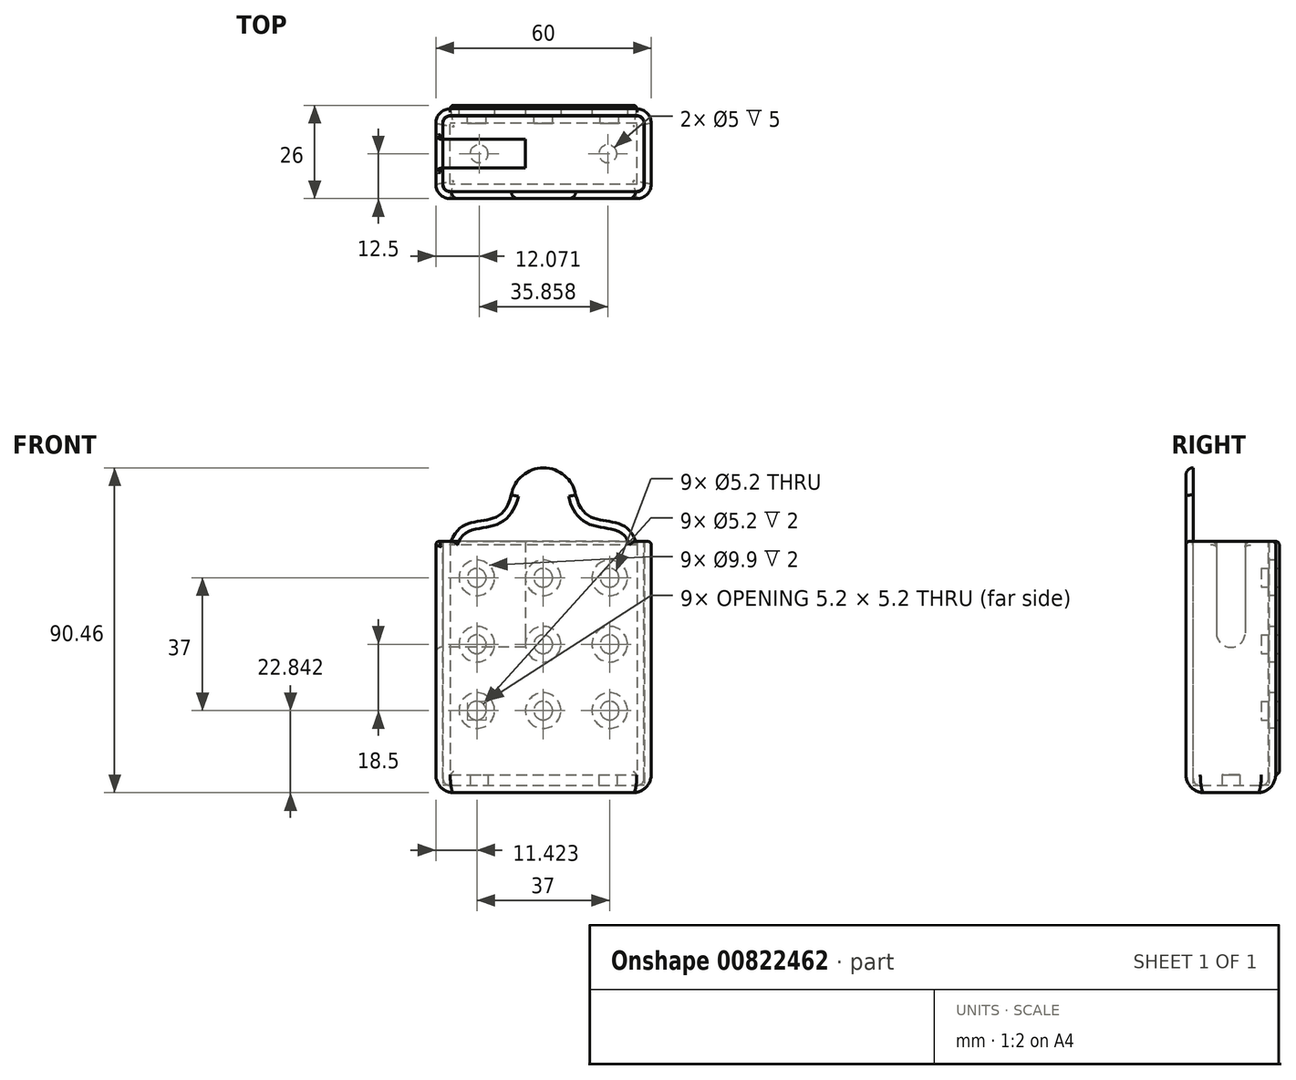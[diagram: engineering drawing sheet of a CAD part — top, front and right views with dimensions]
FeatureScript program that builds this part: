
annotation { "Feature Type Name" : "Feature", "Feature Type Description" : "" }
export const myFeature = defineFeature(function(context is Context, id is Id, definition is map)
    precondition{}
    {
        {
            var Q0;
            Q0=qCreatedBy(makeId("Front.planeOp"),FACE);
            var sketch = newSketch(context, id + "F0", { "sketchPlane" : qUnion([Q0])});
            skPoint(sketch, "E0.middle", {"position": v(0, 0) * mm});
            skLineSegment(sketch, "E1.bottom", {"start": v(28, -42.5) * mm, "end": v(-28, -42.5) * mm});
            skLineSegment(sketch, "E1.top", {"start": v(28, 42.5) * mm, "end": v(-28, 42.5) * mm});
            skLineSegment(sketch, "E1.left", {"start": v(28, -42.5) * mm, "end": v(28, 42.5) * mm});
            skLineSegment(sketch, "E1.right", {"start": v(-28, -42.5) * mm, "end": v(-28, 42.5) * mm});
            skSolve(sketch);
        }
        {
            var Q0;
            Q0=qSketchRegion(id+"F0",true);
            extrude(context, id + "F1", {"entities" : qUnion([Q0]), "endBound" : BoundingType.SYMMETRIC, "depth" : 21 * mm, "offsetDistance" : 25 * mm});
        }
        {
            var Q0;
            Q0=makeQuery(id+"F1.opExtrude","CAP_FACE",FACE,{"disambiguationData":[OSD([sQuery(id+"F0.wireOp",EDGE,"E1.bottom"),sQuery(id+"F0.wireOp",EDGE,"E1.top"),sQuery(id+"F0.wireOp",EDGE,"E1.left"),sQuery(id+"F0.wireOp",EDGE,"E1.right")])],"isStart":false});
            var Q1;
            Q1=makeQuery(id+"F1.opExtrude","CAP_FACE",FACE,{"disambiguationData":[OSD([sQuery(id+"F0.wireOp",EDGE,"E1.bottom"),sQuery(id+"F0.wireOp",EDGE,"E1.top"),sQuery(id+"F0.wireOp",EDGE,"E1.left"),sQuery(id+"F0.wireOp",EDGE,"E1.right")])],"isStart":true});
            var Q2;
            Q2=makeQuery(id+"F1.opExtrude","SWEPT_EDGE",EDGE,{"disambiguationData":[OSD([sQuery(id+"F0.wireOp",EDGE,"E1.bottom"),sQuery(id+"F0.wireOp",EDGE,"E1.left")])]});
            var Q3;
            Q3=makeQuery(id+"F1.opExtrude","SWEPT_EDGE",EDGE,{"disambiguationData":[OSD([sQuery(id+"F0.wireOp",EDGE,"E1.bottom"),sQuery(id+"F0.wireOp",EDGE,"E1.right")])]});
            var Q4;
            Q4=makeQuery(id+"F1.opExtrude","SWEPT_FACE",FACE,{"disambiguationData":[OSD([sQuery(id+"F0.wireOp",EDGE,"E1.top")])]});
            fillet(context, id + "F2", {"entities" : qUnion([Q0, Q1, Q2, Q3, Q4]), "radius" : 2 * mm, "tangentPropagation" : true, "allowEdgeOverflow" : false});
        }
        {
            var Q0;
            Q0=qCreatedBy(makeId("Top.planeOp"),FACE);
            var sketch = newSketch(context, id + "F3", { "sketchPlane" : qUnion([Q0])});
            skArc(sketch, "E2.0", {"start": v(-26, 12.5) * mm, "mid": v(-28.83, 11.33) * mm, "end": v(-30, 8.5) * mm});
            skLineSegment(sketch, "E2.1", {"start": v(-30, -8.5) * mm, "end": v(-30, 8.5) * mm});
            skLineSegment(sketch, "E2.2", {"start": v(-26, 12.5) * mm, "end": v(26, 12.5) * mm});
            skArc(sketch, "E2.3", {"start": v(-30, -8.5) * mm, "mid": v(-28.83, -11.33) * mm, "end": v(-26, -12.5) * mm});
            skArc(sketch, "E2.4", {"start": v(30, 8.5) * mm, "mid": v(28.83, 11.33) * mm, "end": v(26, 12.5) * mm});
            skLineSegment(sketch, "E2.5", {"start": v(30, 8.5) * mm, "end": v(30, -8.5) * mm});
            skArc(sketch, "E2.6", {"start": v(26, -12.5) * mm, "mid": v(28.83, -11.33) * mm, "end": v(30, -8.5) * mm});
            skLineSegment(sketch, "E2.7", {"start": v(26, -12.5) * mm, "end": v(-26, -12.5) * mm});
            skArc(sketch, "E3.0", {"start": v(-26, 10.6) * mm, "mid": v(-27.48, 9.98) * mm, "end": v(-28.1, 8.5) * mm});
            skLineSegment(sketch, "E3.1", {"start": v(-28.1, -8.5) * mm, "end": v(-28.1, 8.5) * mm});
            skLineSegment(sketch, "E3.2", {"start": v(-26, 10.6) * mm, "end": v(26, 10.6) * mm});
            skArc(sketch, "E3.3", {"start": v(-28.1, -8.5) * mm, "mid": v(-27.48, -9.98) * mm, "end": v(-26, -10.6) * mm});
            skArc(sketch, "E3.4", {"start": v(28.1, 8.5) * mm, "mid": v(27.48, 9.98) * mm, "end": v(26, 10.6) * mm});
            skLineSegment(sketch, "E3.5", {"start": v(28.1, 8.5) * mm, "end": v(28.1, -8.5) * mm});
            skArc(sketch, "E3.6", {"start": v(26, -10.6) * mm, "mid": v(27.48, -9.98) * mm, "end": v(28.1, -8.5) * mm});
            skLineSegment(sketch, "E3.7", {"start": v(26, -10.6) * mm, "end": v(-26, -10.6) * mm});
            skSolve(sketch);
        }
        {
            var Q0;
            Q0=makeQuery(id+"F3.imprint","IMPRINT",FACE,{"disambiguationData":[TD([[makeQuery(id+"F3.imprint","IMPRINT",EDGE,{"derivedFrom":sQuery(id+"F3.wireOp",EDGE,"E2.0")}),1.0]])]});
            extrude(context, id + "F4", {"entities" : qUnion([Q0]), "endBound" : BoundingType.SYMMETRIC, "depth" : 85 * mm, "offsetDistance" : 25 * mm});
        }
        {
            var Q0;
            Q0=makeQuery(id+"F4.opExtrude","CAP_FACE",FACE,{"disambiguationData":[OSD([sQuery(id+"F3.wireOp",EDGE,"E2.0"),sQuery(id+"F3.wireOp",EDGE,"E2.1"),sQuery(id+"F3.wireOp",EDGE,"E2.2"),sQuery(id+"F3.wireOp",EDGE,"E2.3"),sQuery(id+"F3.wireOp",EDGE,"E2.4"),sQuery(id+"F3.wireOp",EDGE,"E2.5"),sQuery(id+"F3.wireOp",EDGE,"E2.6"),sQuery(id+"F3.wireOp",EDGE,"E2.7"),sQuery(id+"F3.wireOp",EDGE,"E3.0"),sQuery(id+"F3.wireOp",EDGE,"E3.1"),sQuery(id+"F3.wireOp",EDGE,"E3.2"),sQuery(id+"F3.wireOp",EDGE,"E3.3"),sQuery(id+"F3.wireOp",EDGE,"E3.4"),sQuery(id+"F3.wireOp",EDGE,"E3.5"),sQuery(id+"F3.wireOp",EDGE,"E3.6"),sQuery(id+"F3.wireOp",EDGE,"E3.7")])],"isStart":true});
            var sketch = newSketch(context, id + "F5", { "sketchPlane" : qUnion([Q0])});
            skArc(sketch, "E4.0", {"start": v(30, 8.5) * mm, "mid": v(28.83, 11.33) * mm, "end": v(26, 12.5) * mm});
            skLineSegment(sketch, "E4.1", {"start": v(30, -8.5) * mm, "end": v(30, 8.5) * mm});
            skLineSegment(sketch, "E4.2", {"start": v(26, 12.5) * mm, "end": v(-26, 12.5) * mm});
            skArc(sketch, "E4.3", {"start": v(26, -12.5) * mm, "mid": v(28.83, -11.33) * mm, "end": v(30, -8.5) * mm});
            skArc(sketch, "E4.4", {"start": v(-26, 12.5) * mm, "mid": v(-28.83, 11.33) * mm, "end": v(-30, 8.5) * mm});
            skLineSegment(sketch, "E4.5", {"start": v(-30, 8.5) * mm, "end": v(-30, -8.5) * mm});
            skArc(sketch, "E4.6", {"start": v(-30, -8.5) * mm, "mid": v(-28.83, -11.33) * mm, "end": v(-26, -12.5) * mm});
            skLineSegment(sketch, "E4.7", {"start": v(-26, -12.5) * mm, "end": v(26, -12.5) * mm});
            skSolve(sketch);
        }
        {
            var Q0;
            Q0 = qSketchRegion(id + "F5", true);
            extrude(context, id + "F6", {"entities" : qUnion([Q0]), "operationType" : NewBodyOperationType.ADD, "depth" : 2 * mm, "offsetDistance" : 25 * mm});
        }
        {
            var Q0;
            Q0=makeQuery(id+"F6.opExtrude","CAP_FACE",FACE,{"disambiguationData":[OSD([sQuery(id+"F5.wireOp",EDGE,"E4.0"),sQuery(id+"F5.wireOp",EDGE,"E4.1"),sQuery(id+"F5.wireOp",EDGE,"E4.2"),sQuery(id+"F5.wireOp",EDGE,"E4.3"),sQuery(id+"F5.wireOp",EDGE,"E4.4"),sQuery(id+"F5.wireOp",EDGE,"E4.5"),sQuery(id+"F5.wireOp",EDGE,"E4.6"),sQuery(id+"F5.wireOp",EDGE,"E4.7")])],"isStart":false});
            fillet(context, id + "F7", {"entities" : qUnion([Q0]), "radius" : 5 * mm, "tangentPropagation" : true, "allowEdgeOverflow" : false});
        }
        {
            var Q0;
            Q0=qCreatedBy(makeId("Front.planeOp"),FACE);
            var sketch = newSketch(context, id + "F8", { "sketchPlane" : qUnion([Q0])});
            skLineSegment(sketch, "E5.bottom", {"start": v(-62.47, 73.93) * mm, "end": v(54.88, 73.93) * mm});
            skLineSegment(sketch, "E5.top", {"start": v(-62.47, 25.5) * mm, "end": v(54.88, 25.5) * mm});
            skLineSegment(sketch, "E5.left", {"start": v(-62.47, 73.93) * mm, "end": v(-62.47, 25.5) * mm});
            skLineSegment(sketch, "E5.right", {"start": v(54.88, 73.93) * mm, "end": v(54.88, 25.5) * mm});
            skSolve(sketch);
        }
        {
            var Q0;
            Q0 = qSketchRegion(id + "F8", true);
            extrude(context, id + "F9", {"entities" : qUnion([Q0]), "operationType" : NewBodyOperationType.REMOVE, "depth" : 25 * mm, "offsetDistance" : 25 * mm, "hasSecondDirection" : true, "secondDirectionOppositeDirection" : true, "secondDirectionDepth" : 25 * mm});
        }
        {
            var Q0;
            Q0=makeQuery(id+"F6.boolean.opBoolean","MERGE",FACE,{"derivedFrom":[makeQuery(id+"F4.opExtrude","SWEPT_FACE",FACE,{"disambiguationData":[OSD([sQuery(id+"F3.wireOp",EDGE,"E2.2")])]}),makeQuery(id+"F6.opExtrude","SWEPT_FACE",FACE,{"disambiguationData":[OSD([sQuery(id+"F5.wireOp",EDGE,"E4.7")])]})]});
            var sketch = newSketch(context, id + "F10", { "sketchPlane" : qUnion([Q0])});
            skLineSegment(sketch, "E6.bottom", {"start": v(-26, 25.52) * mm, "end": v(26, 25.52) * mm});
            skLineSegment(sketch, "E6.top", {"start": v(-26, -39.5) * mm, "end": v(26, -39.5) * mm});
            skLineSegment(sketch, "E6.left", {"start": v(-26, 25.52) * mm, "end": v(-26, -39.5) * mm});
            skLineSegment(sketch, "E6.right", {"start": v(26, 25.52) * mm, "end": v(26, -39.5) * mm});
            skSolve(sketch);
        }
        {
            var Q0;
            Q0 = qSketchRegion(id + "F10", true);
            extrude(context, id + "F11", {"entities" : qUnion([Q0]), "operationType" : NewBodyOperationType.ADD, "depth" : 1 * mm, "offsetDistance" : 25 * mm});
        }
        {
            var Q0;
            Q0=makeQuery(id+"F11.opExtrude","CAP_FACE",FACE,{"disambiguationData":[OSD([sQuery(id+"F10.wireOp",EDGE,"E6.bottom"),sQuery(id+"F10.wireOp",EDGE,"E6.top"),sQuery(id+"F10.wireOp",EDGE,"E6.left"),sQuery(id+"F10.wireOp",EDGE,"E6.right")])],"isStart":false});
            var sketch = newSketch(context, id + "F12", { "sketchPlane" : qUnion([Q0])});
            skCircle(sketch, "E7", {"center": v(-18.42, 15.34) * mm, "radius": 2.6 * mm});
            skCircle(sketch, "E8.0.1.0", {"center": v(-18.42, -3.16) * mm, "radius": 2.6 * mm});
            skCircle(sketch, "E8.0.2.0", {"center": v(-18.42, -21.66) * mm, "radius": 2.6 * mm});
            skCircle(sketch, "E8.1.0.0", {"center": v(0.08, 15.34) * mm, "radius": 2.6 * mm});
            skCircle(sketch, "E8.1.1.0", {"center": v(0.08, -3.16) * mm, "radius": 2.6 * mm});
            skCircle(sketch, "E8.1.2.0", {"center": v(0.08, -21.66) * mm, "radius": 2.6 * mm});
            skCircle(sketch, "E8.2.0.0", {"center": v(18.58, 15.34) * mm, "radius": 2.6 * mm});
            skCircle(sketch, "E8.2.1.0", {"center": v(18.58, -3.16) * mm, "radius": 2.6 * mm});
            skCircle(sketch, "E8.2.2.0", {"center": v(18.58, -21.66) * mm, "radius": 2.6 * mm});
            skLineSegment(sketch, "E8.direction1", {"start": v(-18.42, 15.34) * mm, "end": v(0.08, 15.34) * mm, "construction": true});
            skLineSegment(sketch, "E8.direction2", {"start": v(-18.42, 15.34) * mm, "end": v(-18.42, -3.16) * mm, "construction": true});
            skSolve(sketch);
        }
        {
            var Q0;
            Q0 = qSketchRegion(id + "F12", true);
            extrude(context, id + "F13", {"entities" : qUnion([Q0]), "operationType" : NewBodyOperationType.REMOVE, "oppositeDirection" : true, "depth" : 5 * mm, "offsetDistance" : 25 * mm});
        }
        {
            var Q0;
            Q0=makeQuery(id+"F6.opExtrude","CAP_FACE",FACE,{"disambiguationData":[OSD([sQuery(id+"F5.wireOp",EDGE,"E4.0"),sQuery(id+"F5.wireOp",EDGE,"E4.1"),sQuery(id+"F5.wireOp",EDGE,"E4.2"),sQuery(id+"F5.wireOp",EDGE,"E4.3"),sQuery(id+"F5.wireOp",EDGE,"E4.4"),sQuery(id+"F5.wireOp",EDGE,"E4.5"),sQuery(id+"F5.wireOp",EDGE,"E4.6"),sQuery(id+"F5.wireOp",EDGE,"E4.7")])],"isStart":false});
            var sketch = newSketch(context, id + "F14", { "sketchPlane" : qUnion([Q0])});
            skCircle(sketch, "E9", {"center": v(-17.93, 0) * mm, "radius": 2.5 * mm});
            skCircle(sketch, "E10.MirrorC", {"center": v(17.93, 0) * mm, "radius": 2.5 * mm});
            skSolve(sketch);
        }
        {
            var Q0;
            Q0 = qSketchRegion(id + "F14", true);
            extrude(context, id + "F15", {"entities" : qUnion([Q0]), "operationType" : NewBodyOperationType.REMOVE, "oppositeDirection" : true, "depth" : 5 * mm, "offsetDistance" : 25 * mm});
        }
        {
            var Q0;
            Q0=makeQuery(id+"F9.boolean.opBoolean","INTERSECT",EDGE,{"derivedFrom":[makeQuery(id+"F6.boolean.opBoolean","MERGE",FACE,{"derivedFrom":[makeQuery(id+"F4.opExtrude","SWEPT_FACE",FACE,{"disambiguationData":[OSD([sQuery(id+"F3.wireOp",EDGE,"E2.7")])]}),makeQuery(id+"F6.opExtrude","SWEPT_FACE",FACE,{"disambiguationData":[OSD([sQuery(id+"F5.wireOp",EDGE,"E4.2")])]})]}),makeQuery(id+"F9.opExtrude","SWEPT_FACE",FACE,{"disambiguationData":[OSD([sQuery(id+"F8.wireOp",EDGE,"E5.top")])]})]});
            fillet(context, id + "F16", {"entities" : qUnion([Q0]), "radius" : 1 * mm, "tangentPropagation" : true, "allowEdgeOverflow" : false});
        }
        {
            var Q0;
            Q0=makeQuery(id+"F6.boolean.opBoolean","MERGE",FACE,{"derivedFrom":[makeQuery(id+"F4.opExtrude","SWEPT_FACE",FACE,{"disambiguationData":[OSD([sQuery(id+"F3.wireOp",EDGE,"E2.1")])]}),makeQuery(id+"F6.opExtrude","SWEPT_FACE",FACE,{"disambiguationData":[OSD([sQuery(id+"F5.wireOp",EDGE,"E4.5")])]})]});
            var sketch = newSketch(context, id + "F17", { "sketchPlane" : qUnion([Q0])});
            skLineSegment(sketch, "E11", {"start": v(0, 31.44) * mm, "end": v(0, 0) * mm, "construction": true});
            skArc(sketch, "E12.0.startCap", {"start": v(-4, 31.44) * mm, "mid": v(0, 35.44) * mm, "end": v(4, 31.44) * mm});
            skArc(sketch, "E12.0.endCap", {"start": v(4, 0) * mm, "mid": v(0, -4) * mm, "end": v(-4, 0) * mm});
            skLineSegment(sketch, "E12.0.left", {"start": v(4, 31.44) * mm, "end": v(4, 0) * mm});
            skLineSegment(sketch, "E12.0.right", {"start": v(-4, 31.44) * mm, "end": v(-4, 0) * mm});
            skSolve(sketch);
        }
        {
            var Q0;
            Q0 = qSketchRegion(id + "F17", true);
            extrude(context, id + "F18", {"entities" : qUnion([Q0]), "operationType" : NewBodyOperationType.REMOVE, "oppositeDirection" : true, "depth" : 25 * mm, "offsetDistance" : 25 * mm});
        }
        {
            var Q0;
            Q0=makeQuery(id+"F18.boolean.opBoolean","INTERSECT",EDGE,{"derivedFrom":[makeQuery(id+"F9.boolean.opBoolean","COPY",FACE,{"disambiguationData":[TD([makeQuery(id+"F4.opExtrude","SWEPT_FACE",FACE,{"disambiguationData":[OSD([sQuery(id+"F3.wireOp",EDGE,"E2.0")])]})])],"derivedFrom":makeQuery(id+"F9.opExtrude","SWEPT_FACE",FACE,{"disambiguationData":[OSD([sQuery(id+"F8.wireOp",EDGE,"E5.top")])]})}),makeQuery(id+"F18.opExtrude","SWEPT_FACE",FACE,{"disambiguationData":[OSD([sQuery(id+"F17.wireOp",EDGE,"E12.0.right")])]})]});
            fillet(context, id + "F19", {"entities" : qUnion([Q0]), "radius" : 1.6 * mm, "tangentPropagation" : true, "allowEdgeOverflow" : false});
        }
        {
            var Q0;
            Q0=makeQuery(id+"F11.opExtrude","CAP_EDGE",EDGE,{"disambiguationData":[OSD([sQuery(id+"F10.wireOp",EDGE,"E6.top")])],"isStart":false});
            var Q1;
            Q1=makeQuery(id+"F11.opExtrude","CAP_EDGE",EDGE,{"disambiguationData":[OSD([sQuery(id+"F10.wireOp",EDGE,"E6.left")])],"isStart":false});
            var Q2;
            Q2=makeQuery(id+"F11.opExtrude","CAP_EDGE",EDGE,{"disambiguationData":[OSD([sQuery(id+"F10.wireOp",EDGE,"E6.right")])],"isStart":false});
            var Q3;
            Q3=makeQuery(id+"F11.opExtrude","CAP_EDGE",EDGE,{"disambiguationData":[OSD([sQuery(id+"F10.wireOp",EDGE,"E6.bottom")])],"isStart":false});
            fillet(context, id + "F20", {"entities" : qUnion([Q0, Q1, Q2, Q3]), "radius" : 1 * mm, "tangentPropagation" : true, "allowEdgeOverflow" : false});
        }
        {
            var Q0;
            Q0=makeQuery(id+"F4.opExtrude","SWEPT_FACE",FACE,{"disambiguationData":[OSD([sQuery(id+"F3.wireOp",EDGE,"E3.2")])]});
            var sketch = newSketch(context, id + "F21", { "sketchPlane" : qUnion([Q0])});
            skCircle(sketch, "E13", {"center": v(-18.58, 15.34) * mm, "radius": 4.95 * mm});
            skCircle(sketch, "E14", {"center": v(-0.08, 15.34) * mm, "radius": 4.95 * mm});
            skCircle(sketch, "E15", {"center": v(18.42, 15.34) * mm, "radius": 4.95 * mm});
            skCircle(sketch, "E16", {"center": v(-18.58, -3.16) * mm, "radius": 4.95 * mm});
            skCircle(sketch, "E17", {"center": v(-0.08, -3.16) * mm, "radius": 4.95 * mm});
            skCircle(sketch, "E18", {"center": v(18.42, -3.16) * mm, "radius": 4.95 * mm});
            skCircle(sketch, "E19", {"center": v(18.42, -21.66) * mm, "radius": 4.95 * mm});
            skCircle(sketch, "E20", {"center": v(-0.08, -21.66) * mm, "radius": 4.95 * mm});
            skCircle(sketch, "E21", {"center": v(-18.58, -21.66) * mm, "radius": 4.95 * mm});
            skSolve(sketch);
        }
        {
            var Q0;
            Q0 = qSketchRegion(id + "F21", true);
            extrude(context, id + "F22", {"entities" : qUnion([Q0]), "operationType" : NewBodyOperationType.REMOVE, "oppositeDirection" : true, "depth" : 2 * mm, "offsetDistance" : 25 * mm});
        }
        {
            var Q0;
            Q0=makeQuery(id+"F6.boolean.opBoolean","MERGE",FACE,{"derivedFrom":[makeQuery(id+"F4.opExtrude","SWEPT_FACE",FACE,{"disambiguationData":[OSD([sQuery(id+"F3.wireOp",EDGE,"E2.7")])]}),makeQuery(id+"F6.opExtrude","SWEPT_FACE",FACE,{"disambiguationData":[OSD([sQuery(id+"F5.wireOp",EDGE,"E4.2")])]})]});
            var sketch = newSketch(context, id + "F23", { "sketchPlane" : qUnion([Q0])});
            skArc(sketch, "E22", {"start": v(8.97, 38.43) * mm, "mid": v(0, 45.96) * mm, "end": v(-8.97, 38.43) * mm});
            skFitSpline(sketch, "E23", {"points": [v(-26, 24.5) * mm, v(-8.97, 38.43) * mm], "startDerivative": vector(9.35, 34.08) * mm, "endDerivative": vector(8.44, 36.23) * mm});
            skFitSpline(sketch, "E24.MirrorCS", {"points": [v(26, 24.5) * mm, v(8.97, 38.43) * mm], "startDerivative": vector(-9.35, 34.08) * mm, "endDerivative": vector(-8.44, 36.23) * mm});
            skSolve(sketch);
        }
        {
            var Q0;
            Q0 = qSketchRegion(id + "F23", true);
            var Q1;
            Q1=makeQuery(id+"F23.imprint","IMPRINT",FACE,{"disambiguationData":[TD([[makeQuery(id+"F23.imprint","IMPRINT",EDGE,{"derivedFrom":sQuery(id+"F23.wireOp",EDGE,"E22")}),1.0]])]});
            extrude(context, id + "F24", {"entities" : qUnion([Q0, Q1]), "operationType" : NewBodyOperationType.ADD, "oppositeDirection" : true, "depth" : 2 * mm, "offsetDistance" : 25 * mm});
        }
        {
            var Q0;
            Q0=makeQuery(id+"F24.opExtrude","CAP_EDGE",EDGE,{"disambiguationData":[OSD([sQuery(id+"F23.wireOp",EDGE,"E22")])],"isStart":true});
            fillet(context, id + "F25", {"entities" : qUnion([Q0]), "radius" : 2 * mm, "tangentPropagation" : true, "allowEdgeOverflow" : false});
        }
    });
